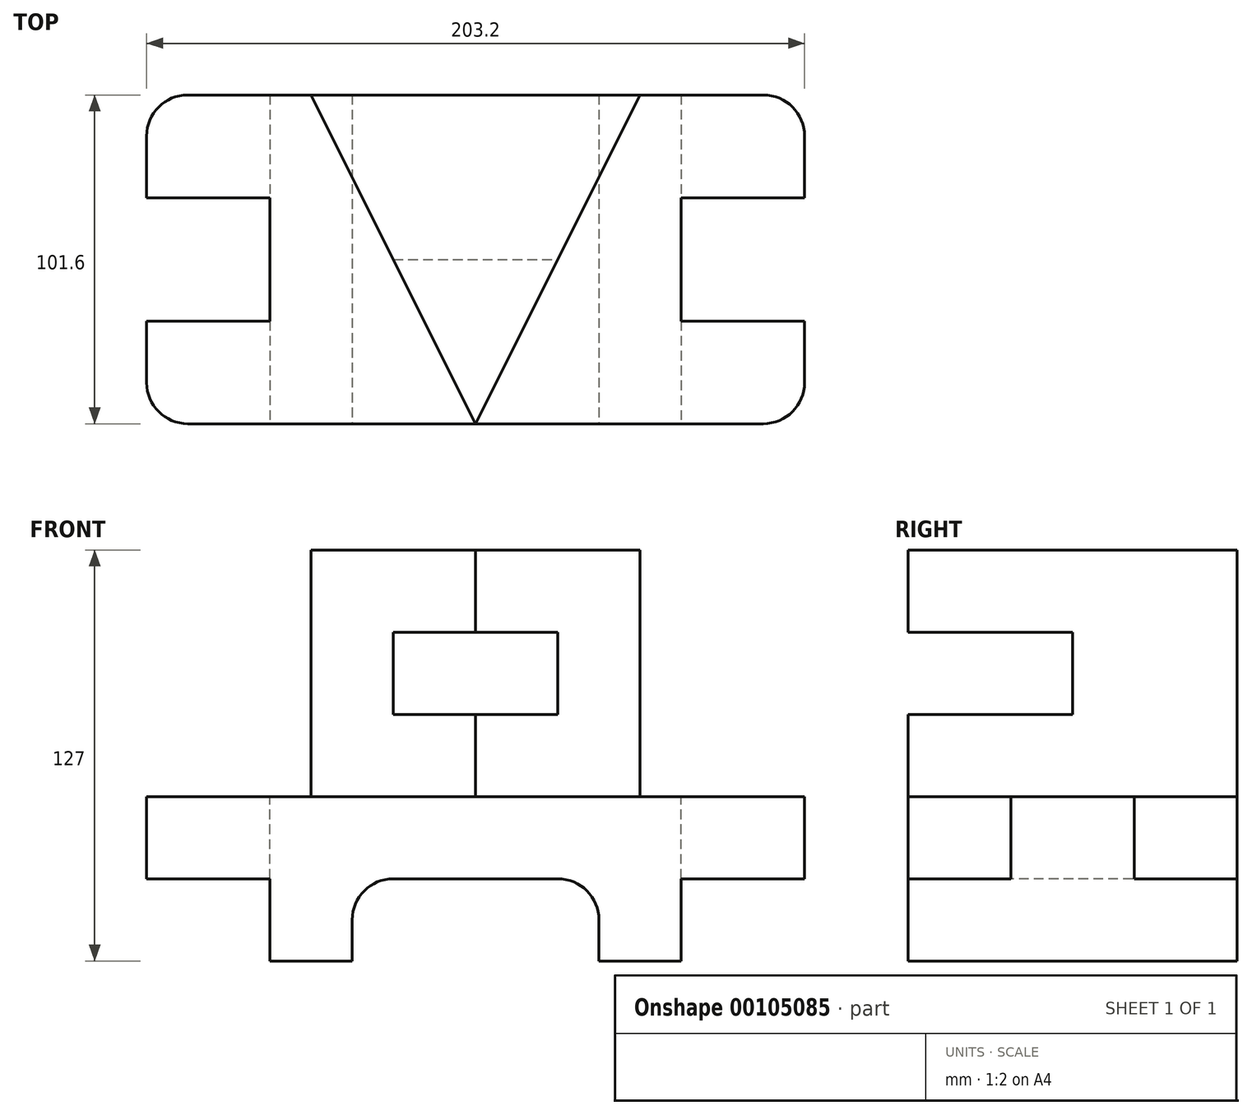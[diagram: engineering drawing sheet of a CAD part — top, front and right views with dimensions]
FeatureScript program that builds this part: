
annotation { "Feature Type Name" : "Feature", "Feature Type Description" : "" }
export const myFeature = defineFeature(function(context is Context, id is Id, definition is map)
    precondition{}
    {
        {
            var Q0;
            Q0=qCreatedBy(makeId("Front.planeOp"),FACE);
            var sketch = newSketch(context, id + "F0", { "sketchPlane" : qUnion([Q0])});
            skLineSegment(sketch, "E0.bottom", {"start": v(0, 0) * mm, "end": v(203.2, 0) * mm});
            skLineSegment(sketch, "E0.top", {"start": v(0, 127) * mm, "end": v(203.2, 127) * mm});
            skLineSegment(sketch, "E0.left", {"start": v(0, 0) * mm, "end": v(0, 127) * mm});
            skLineSegment(sketch, "E0.right", {"start": v(203.2, 0) * mm, "end": v(203.2, 127) * mm});
            skSolve(sketch);
        }
        {
            var Q0;
            Q0 = qSketchRegion(id + "F0", true);
            extrude(context, id + "F1", {"entities" : qUnion([Q0]), "depth" : 101.6 * mm});
        }
        {
            var Q0;
            Q0=makeQuery(id+"F1.opExtrude","CAP_FACE",FACE,{"disambiguationData":[OSD([sQuery(id+"F0.wireOp",EDGE,"E0.bottom"),sQuery(id+"F0.wireOp",EDGE,"E0.top"),sQuery(id+"F0.wireOp",EDGE,"E0.left"),sQuery(id+"F0.wireOp",EDGE,"E0.right")])],"isStart":false});
            var sketch = newSketch(context, id + "F2", { "sketchPlane" : qUnion([Q0])});
            skLineSegment(sketch, "E1.bottom", {"start": v(0, 25.4) * mm, "end": v(38.1, 25.4) * mm});
            skLineSegment(sketch, "E1.top", {"start": v(0, 0) * mm, "end": v(38.1, 0) * mm});
            skLineSegment(sketch, "E1.left", {"start": v(0, 25.4) * mm, "end": v(0, 0) * mm});
            skLineSegment(sketch, "E1.right", {"start": v(38.1, 25.4) * mm, "end": v(38.1, 0) * mm});
            skLineSegment(sketch, "E2.bottom", {"start": v(63.5, 0) * mm, "end": v(139.7, 0) * mm});
            skLineSegment(sketch, "E2.top", {"start": v(76.2, 25.4) * mm, "end": v(127, 25.4) * mm});
            skLineSegment(sketch, "E2.left", {"start": v(63.5, 0) * mm, "end": v(63.5, 12.7) * mm});
            skLineSegment(sketch, "E2.right", {"start": v(139.7, 0) * mm, "end": v(139.7, 12.7) * mm});
            skLineSegment(sketch, "E3.bottom", {"start": v(165.1, 0) * mm, "end": v(203.2, 0) * mm});
            skLineSegment(sketch, "E3.top", {"start": v(165.1, 25.4) * mm, "end": v(203.2, 25.4) * mm});
            skLineSegment(sketch, "E3.left", {"start": v(165.1, 0) * mm, "end": v(165.1, 25.4) * mm});
            skLineSegment(sketch, "E3.right", {"start": v(203.2, 0) * mm, "end": v(203.2, 25.4) * mm});
            skPoint(sketch, "E4.visualSharp", {"position": v(63.5, 25.4) * mm});
            skArc(sketch, "E4.filletArc", {"start": v(76.2, 25.4) * mm, "mid": v(67.22, 21.68) * mm, "end": v(63.5, 12.7) * mm});
            skPoint(sketch, "E5.visualSharp", {"position": v(139.7, 25.4) * mm});
            skArc(sketch, "E5.filletArc", {"start": v(139.7, 12.7) * mm, "mid": v(135.98, 21.68) * mm, "end": v(127, 25.4) * mm});
            skSolve(sketch);
        }
        {
            var Q0;
            Q0 = qSketchRegion(id + "F2", true);
            extrude(context, id + "F3", {"entities" : qUnion([Q0]), "operationType" : NewBodyOperationType.REMOVE, "endBound" : BoundingType.THROUGH_ALL, "oppositeDirection" : true, "depth" : 25.4 * mm});
        }
        {
            var Q0;
            Q0=makeQuery(id+"F1.opExtrude","SWEPT_FACE",FACE,{"disambiguationData":[OSD([sQuery(id+"F0.wireOp",EDGE,"E0.top")])]});
            var sketch = newSketch(context, id + "F4", { "sketchPlane" : qUnion([Q0])});
            skLineSegment(sketch, "E6", {"start": v(101.6, -101.6) * mm, "end": v(152.4, 0) * mm});
            skPoint(sketch, "E7.endSnap0", {"position": v(101.6, 0) * mm});
            skLineSegment(sketch, "E8", {"start": v(50.8, 0) * mm, "end": v(101.6, -101.6) * mm});
            skLineSegment(sketch, "E9", {"start": v(50.8, 0) * mm, "end": v(152.4, 0) * mm});
            skLineSegment(sketch, "E10.bottom", {"start": v(0, 0) * mm, "end": v(203.2, 0) * mm});
            skLineSegment(sketch, "E10.top", {"start": v(0, -101.6) * mm, "end": v(203.2, -101.6) * mm});
            skLineSegment(sketch, "E10.left", {"start": v(0, 0) * mm, "end": v(0, -101.6) * mm});
            skLineSegment(sketch, "E10.right", {"start": v(203.2, 0) * mm, "end": v(203.2, -101.6) * mm});
            skSolve(sketch);
        }
        {
            var Q0;
            Q0=makeQuery(id+"F1.opExtrude","SWEPT_FACE",FACE,{"disambiguationData":[OSD([sQuery(id+"F0.wireOp",EDGE,"E0.right")])]});
            var sketch = newSketch(context, id + "F5", { "sketchPlane" : qUnion([Q0])});
            skLineSegment(sketch, "E11.bottom", {"start": v(-101.6, 101.6) * mm, "end": v(-50.8, 101.6) * mm});
            skLineSegment(sketch, "E11.top", {"start": v(-101.6, 76.2) * mm, "end": v(-50.8, 76.2) * mm});
            skLineSegment(sketch, "E11.left", {"start": v(-101.6, 101.6) * mm, "end": v(-101.6, 76.2) * mm});
            skLineSegment(sketch, "E11.right", {"start": v(-50.8, 101.6) * mm, "end": v(-50.8, 76.2) * mm});
            skSolve(sketch);
        }
        {
            var Q0;
            Q0 = qSketchRegion(id + "F5", true);
            extrude(context, id + "F6", {"entities" : qUnion([Q0]), "operationType" : NewBodyOperationType.REMOVE, "endBound" : BoundingType.THROUGH_ALL, "oppositeDirection" : true, "depth" : 25.4 * mm});
        }
        {
            var Q0;
            {var subQ0=sQuery(id+"F4.wireOp",EDGE,"E8");Q0=makeQuery(id+"F4.imprint","IMPRINT",FACE,{"disambiguationData":[TD([[makeQuery(id+"F4.imprint","IMPRINT",EDGE,{"derivedFrom":subQ0}),-1.0]])]});}
            var Q1;
            {var subQ0=sQuery(id+"F4.wireOp",EDGE,"E6");Q1=makeQuery(id+"F4.imprint","IMPRINT",FACE,{"disambiguationData":[TD([[makeQuery(id+"F4.imprint","IMPRINT",EDGE,{"derivedFrom":subQ0}),-1.0]])]});}
            extrude(context, id + "F7", {"entities" : qUnion([Q0, Q1]), "operationType" : NewBodyOperationType.REMOVE, "oppositeDirection" : true, "depth" : 76.2 * mm});
        }
        {
            var Q0;
            Q0=makeQuery(id+"F7.boolean.opBoolean","COPY",FACE,{"derivedFrom":makeQuery(id+"F7.opExtrude","CAP_FACE",FACE,{"disambiguationData":[OSD([sQuery(id+"F4.wireOp",EDGE,"E8"),sQuery(id+"F4.wireOp",EDGE,"E10.bottom"),sQuery(id+"F4.wireOp",EDGE,"E10.top"),sQuery(id+"F4.wireOp",EDGE,"E10.left")])],"isStart":false})});
            var sketch = newSketch(context, id + "F8", { "sketchPlane" : qUnion([Q0])});
            skLineSegment(sketch, "E12.bottom", {"start": v(12.7, 0) * mm, "end": v(12.7, 0) * mm});
            skLineSegment(sketch, "E12.top", {"start": v(0, -12.7) * mm, "end": v(12.7, -12.7) * mm});
            skLineSegment(sketch, "E12.left", {"start": v(0, -12.7) * mm, "end": v(0, -12.7) * mm});
            skLineSegment(sketch, "E12.right", {"start": v(12.7, 0) * mm, "end": v(12.7, -12.7) * mm});
            skLineSegment(sketch, "E13.bottom", {"start": v(12.7, -101.6) * mm, "end": v(12.7, -101.6) * mm});
            skLineSegment(sketch, "E13.top", {"start": v(0, -88.9) * mm, "end": v(12.7, -88.9) * mm});
            skLineSegment(sketch, "E13.left", {"start": v(0, -88.9) * mm, "end": v(0, -88.9) * mm});
            skLineSegment(sketch, "E13.right", {"start": v(12.7, -101.6) * mm, "end": v(12.7, -88.9) * mm});
            skLineSegment(sketch, "E14.bottom", {"start": v(0, -31.75) * mm, "end": v(38.1, -31.75) * mm});
            skLineSegment(sketch, "E14.top", {"start": v(0, -69.85) * mm, "end": v(38.1, -69.85) * mm});
            skLineSegment(sketch, "E14.left", {"start": v(0, -31.75) * mm, "end": v(0, -69.85) * mm});
            skLineSegment(sketch, "E14.right", {"start": v(38.1, -31.75) * mm, "end": v(38.1, -69.85) * mm});
            skPoint(sketch, "E15.visualSharp", {"position": v(0, 0) * mm});
            skArc(sketch, "E15.filletArc", {"start": v(12.7, 0) * mm, "mid": v(3.72, -3.72) * mm, "end": v(0, -12.7) * mm});
            skPoint(sketch, "E16.visualSharp", {"position": v(0, -101.6) * mm});
            skArc(sketch, "E16.filletArc", {"start": v(0, -88.9) * mm, "mid": v(3.72, -97.88) * mm, "end": v(12.7, -101.6) * mm});
            skSolve(sketch);
        }
        {
            var Q0;
            Q0=makeQuery(id+"F8.imprint","IMPRINT",FACE,{"disambiguationData":[TD([[makeQuery(id+"F8.imprint","IMPRINT",EDGE,{"derivedFrom":sQuery(id+"F8.wireOp",EDGE,"E14.bottom")}),-1.0]])]});
            var Q1;
            {var subQ0=sQuery(id+"F8.wireOp",EDGE,"E15.filletArc");Q1=makeQuery(id+"F8.imprint","IMPRINT",FACE,{"disambiguationData":[TD([[makeQuery(id+"F8.imprint","IMPRINT",EDGE,{"derivedFrom":subQ0}),-1.0]])]});}
            var Q2;
            {var subQ0=sQuery(id+"F8.wireOp",EDGE,"E16.filletArc");Q2=makeQuery(id+"F8.imprint","IMPRINT",FACE,{"disambiguationData":[TD([[makeQuery(id+"F8.imprint","IMPRINT",EDGE,{"derivedFrom":subQ0}),-1.0]])]});}
            extrude(context, id + "F9", {"entities" : qUnion([Q0, Q1, Q2]), "operationType" : NewBodyOperationType.REMOVE, "endBound" : BoundingType.THROUGH_ALL, "oppositeDirection" : true, "depth" : 25.4 * mm});
        }
        {
            var Q0;
            Q0=makeQuery(id+"F7.boolean.opBoolean","COPY",FACE,{"derivedFrom":makeQuery(id+"F7.opExtrude","CAP_FACE",FACE,{"disambiguationData":[OSD([sQuery(id+"F4.wireOp",EDGE,"E6"),sQuery(id+"F4.wireOp",EDGE,"E10.bottom"),sQuery(id+"F4.wireOp",EDGE,"E10.top"),sQuery(id+"F4.wireOp",EDGE,"E10.right")])],"isStart":false})});
            var sketch = newSketch(context, id + "F10", { "sketchPlane" : qUnion([Q0])});
            skLineSegment(sketch, "E17.bottom", {"start": v(190.5, 0) * mm, "end": v(190.5, 0) * mm});
            skLineSegment(sketch, "E17.top", {"start": v(203.2, -12.7) * mm, "end": v(190.5, -12.7) * mm});
            skLineSegment(sketch, "E17.left", {"start": v(203.2, -12.7) * mm, "end": v(203.2, -12.7) * mm});
            skLineSegment(sketch, "E17.right", {"start": v(190.5, 0) * mm, "end": v(190.5, -12.7) * mm});
            skLineSegment(sketch, "E18.bottom", {"start": v(190.5, -101.6) * mm, "end": v(190.5, -101.6) * mm});
            skLineSegment(sketch, "E18.top", {"start": v(203.2, -88.9) * mm, "end": v(190.5, -88.9) * mm});
            skLineSegment(sketch, "E18.left", {"start": v(203.2, -88.9) * mm, "end": v(203.2, -88.9) * mm});
            skLineSegment(sketch, "E18.right", {"start": v(190.5, -101.6) * mm, "end": v(190.5, -88.9) * mm});
            skLineSegment(sketch, "E19.bottom", {"start": v(203.2, -31.75) * mm, "end": v(165.1, -31.75) * mm});
            skLineSegment(sketch, "E19.top", {"start": v(203.2, -69.85) * mm, "end": v(165.1, -69.85) * mm});
            skLineSegment(sketch, "E19.left", {"start": v(203.2, -31.75) * mm, "end": v(203.2, -69.85) * mm});
            skLineSegment(sketch, "E19.right", {"start": v(165.1, -31.75) * mm, "end": v(165.1, -69.85) * mm});
            skPoint(sketch, "E20.visualSharp", {"position": v(203.2, 0) * mm});
            skArc(sketch, "E20.filletArc", {"start": v(203.2, -12.7) * mm, "mid": v(199.48, -3.72) * mm, "end": v(190.5, 0) * mm});
            skPoint(sketch, "E21.visualSharp", {"position": v(203.2, -101.6) * mm});
            skArc(sketch, "E21.filletArc", {"start": v(190.5, -101.6) * mm, "mid": v(199.48, -97.88) * mm, "end": v(203.2, -88.9) * mm});
            skSolve(sketch);
        }
        {
            var Q0;
            Q0=makeQuery(id+"F10.imprint","IMPRINT",FACE,{"disambiguationData":[TD([[makeQuery(id+"F10.imprint","IMPRINT",EDGE,{"derivedFrom":sQuery(id+"F10.wireOp",EDGE,"E19.bottom")}),1.0]])]});
            var Q1;
            {var subQ0=sQuery(id+"F10.wireOp",EDGE,"E21.filletArc");Q1=makeQuery(id+"F10.imprint","IMPRINT",FACE,{"disambiguationData":[TD([[makeQuery(id+"F10.imprint","IMPRINT",EDGE,{"derivedFrom":subQ0}),-1.0]])]});}
            var Q2;
            {var subQ0=sQuery(id+"F10.wireOp",EDGE,"E20.filletArc");Q2=makeQuery(id+"F10.imprint","IMPRINT",FACE,{"disambiguationData":[TD([[makeQuery(id+"F10.imprint","IMPRINT",EDGE,{"derivedFrom":subQ0}),-1.0]])]});}
            extrude(context, id + "F11", {"entities" : qUnion([Q0, Q1, Q2]), "operationType" : NewBodyOperationType.REMOVE, "endBound" : BoundingType.THROUGH_ALL, "oppositeDirection" : true, "depth" : 25.4 * mm});
        }
    });
